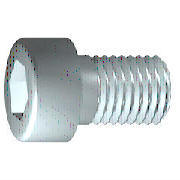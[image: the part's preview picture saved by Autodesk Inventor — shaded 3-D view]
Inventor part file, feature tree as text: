
AUTODESK INVENTOR PART (.ipt)
format: ipt  version: 2022 (Build 260153000, 153)  size: 194,560 bytes
history: native  units: mm (DEFAULTED — no unit token found)
features: sketch x2, other x1, extrude x1, plane x1, fillet x1
ambient origin geometry x7: Origin, YZ Plane, XY Plane, X Axis, Y Axis, Z Axis, Center Point
bodies: Solid1 (feature_tree)
feature tree (6):
  other  "Базовый элемент"
  extrude  "Паз"  Depth=8.75mm
  plane  "Work Plane1"
  fillet  "Fillet2"  Radius=0.306825mm
  sketch  "Эскиз1"
  sketch  "Эскиз2"
